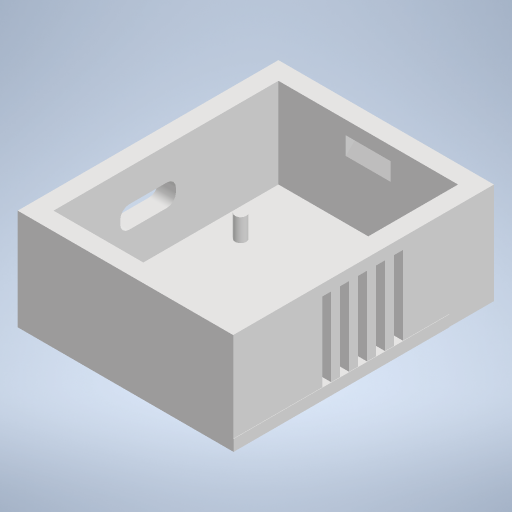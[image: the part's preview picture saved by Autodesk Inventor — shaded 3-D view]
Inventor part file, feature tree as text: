
AUTODESK INVENTOR PART (.ipt)
format: ipt  version: 2024 (Build 280153000, 153)  size: 329,216 bytes
history: native  units: mm
features: extrude x9, sketch x9, chamfer x2, fillet x1
ambient origin geometry x8: Origin, YZ Plane, XZ Plane, XY Plane, X Axis, Y Axis, Z Axis, Center Point
bodies: Volumenkörper1 (feature_tree)
feature tree (21):
  extrude  "Extrusion1"  Depth=48.1mm
  extrude  "Extrusion2"  Depth=4.0mm
  extrude  "Extrusion3"  Depth=4.0mm
  extrude  "Extrusion4"  Depth=4.0mm
  extrude  "Extrusion5"  Depth=4.0mm
  extrude  "Extrusion6"  Depth=2.5mm
  fillet  "Rundung1"  Radius=2.5mm
  extrude  "Extrusion7"  Depth=2.5mm TaperAngle=0.0deg
  extrude  "Extrusion8"  Depth=10.0mm TaperAngle=0.0deg
  chamfer  "Fasen1"  Distance=4.0mm
  extrude  "Extrusion9"  Depth=4.0mm
  chamfer  "Fasen2"  Distance=4.0mm
  sketch  "Skizze2"  dims[d6=48.1mm d7=48.1mm]
  sketch  "Skizze3"  dims[d8=4.0mm d9=4.0mm]
  sketch  "Skizze4"  dims[d10=4.0mm d11=4.0mm]
  sketch  "Skizze5"  dims[d12=2.5mm d13=0.0mm d14=4.0mm]
  sketch  "Skizze6"  dims[d15=4.0mm d16=4.0mm]
  sketch  "Skizze8"  dims[d17=4.0mm d18=2.5mm d19=2.5mm]
  sketch  "Skizze9"  dims[d20=2.5mm d21=2.5mm d22=0.0mm]
  sketch  "Skizze10"  dims[d23=2.5mm d24=0.0mm d25=10.0mm d26=0.0mm]
  sketch  "Skizze12"  dims[d27=4.0mm d28=4.0mm d29=4.0mm d30=4.0mm d31=20.0mm d32=0.0mm d33=20.0mm d34=0.0mm d35=2.0mm d36=2.5mm d38=2.0mm d39=2.0mm d40=2.0mm d41=2.0mm d42=2.0mm d43=2.0mm d44=2.0mm d45=2.0mm d46=2.0mm d47=20.0mm d48=0.0mm d49=20.0mm d50=5.0mm d51=10.0mm d52=4.0mm d53=2.0mm d54=2.0mm d55=0.0mm d56=2.0mm d57=2.0mm d58=45.0deg d59=20.0mm d60=5.0mm d61=10.0mm d62=4.0mm d63=2.0mm d64=0.0mm d65=2.0mm d66=2.0mm d67=45.0deg]
